# Revit family: Shower-Shower_Trim-KOHLER-Refinia-K-TLS5320
name_source: partatom
category: Plumbing Fixtures
revit_build: Autodesk Revit 2015 (Build: 20140606_1530(x64)
units: mm (PartAtom-declared; Revit-internal decimal feet)

## types (2) — shared parameters
ADA Compliant = Yes
Assembly Code = D2010700
CW Connection = No
Cold Water Inlet = Cold Water Inlet
Date Modified = 2/4/2019
Default Elevation = 42"
Description = Rite-Temp shower valve trim with lever handle, less showerhead
Drain Included = No
HW Connection = Yes
Handle Clearance = 3 5/16"
Height = 6 7/16"
Hot Water Inlet = Hot Water Inlet
Length = 4 1/2"
Manufacturer = KOHLER Co.
MasterFormat 1995 = 15410
MasterFormat 2004 = 22.41.23
Material = Premium Metal Construction
Product Documentation Link = https://www.us.kohler.com
Product Name = Refinia
Product Page URL = http://www.us.kohler.com
Tempered Water Inlet = Tempered Water Inlet
URL = https://www.us.kohler.com
Vent Connection = No
Waste Connection = No
Waste Water Outlet = Waste Water Outlet
WaterSense Certified = No
Width = 6 7/16"

## per-type parameters (varying)
| type | Finish | Model | Type |
| BN-Vibrant Brushed Nickel | Kohler-Metal-BN-Vibrant_Brushed_Nickel | K-TLS5320-4-BN | 2 |
| CP-Polished Chrome | Kohler-Metal-CP-Polished_Chrome | K-TLS5320-4-CP | 1 |

## geometry (parser evidence)
native form markers: Sweep x9
no freeform markers — native parametric forms only
